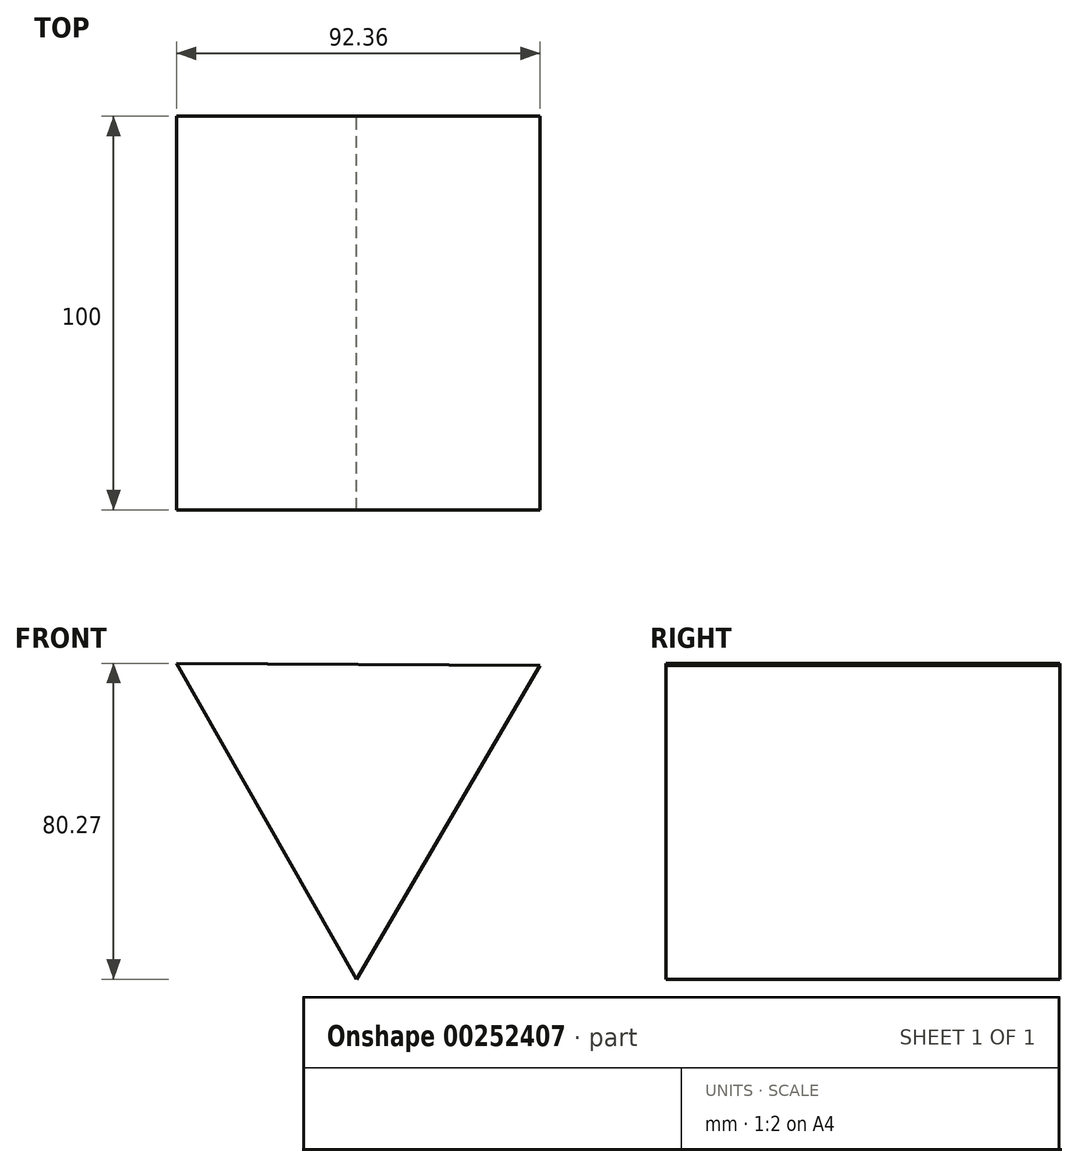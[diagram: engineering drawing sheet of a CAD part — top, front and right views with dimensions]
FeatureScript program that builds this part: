
annotation { "Feature Type Name" : "Feature", "Feature Type Description" : "" }
export const myFeature = defineFeature(function(context is Context, id is Id, definition is map)
    precondition{}
    {
        {
            var Q0;
            Q0=qCreatedBy(makeId("Front.planeOp"),FACE);
            var sketch = newSketch(context, id + "F0", { "sketchPlane" : qUnion([Q0])});
            skCircle(sketch, "E0.cCircle", {"center": v(0, 0) * mm, "radius": 53.33 * mm, "construction": true});
            skLineSegment(sketch, "E0.0", {"start": v(46.34, 26.38) * mm, "end": v(-0.33, -53.32) * mm});
            skLineSegment(sketch, "E0.1", {"start": v(-0.33, -53.32) * mm, "end": v(-46.02, 26.95) * mm});
            skLineSegment(sketch, "E0.2", {"start": v(-46.02, 26.95) * mm, "end": v(46.34, 26.38) * mm});
            skSolve(sketch);
        }
        {
            var Q0;
            Q0 = qSketchRegion(id + "F0", true);
            var Q1;
            Q1=makeQuery(id+"F0.imprint","IMPRINT",FACE,{"disambiguationData":[TD([[makeQuery(id+"F0.imprint","IMPRINT",EDGE,{"derivedFrom":sQuery(id+"F0.wireOp",EDGE,"E0.0")}),-1.0]])]});
            extrude(context, id + "F1", {"entities" : qUnion([Q0, Q1]), "endBound" : BoundingType.SYMMETRIC, "depth" : 100 * mm});
        }
    });
